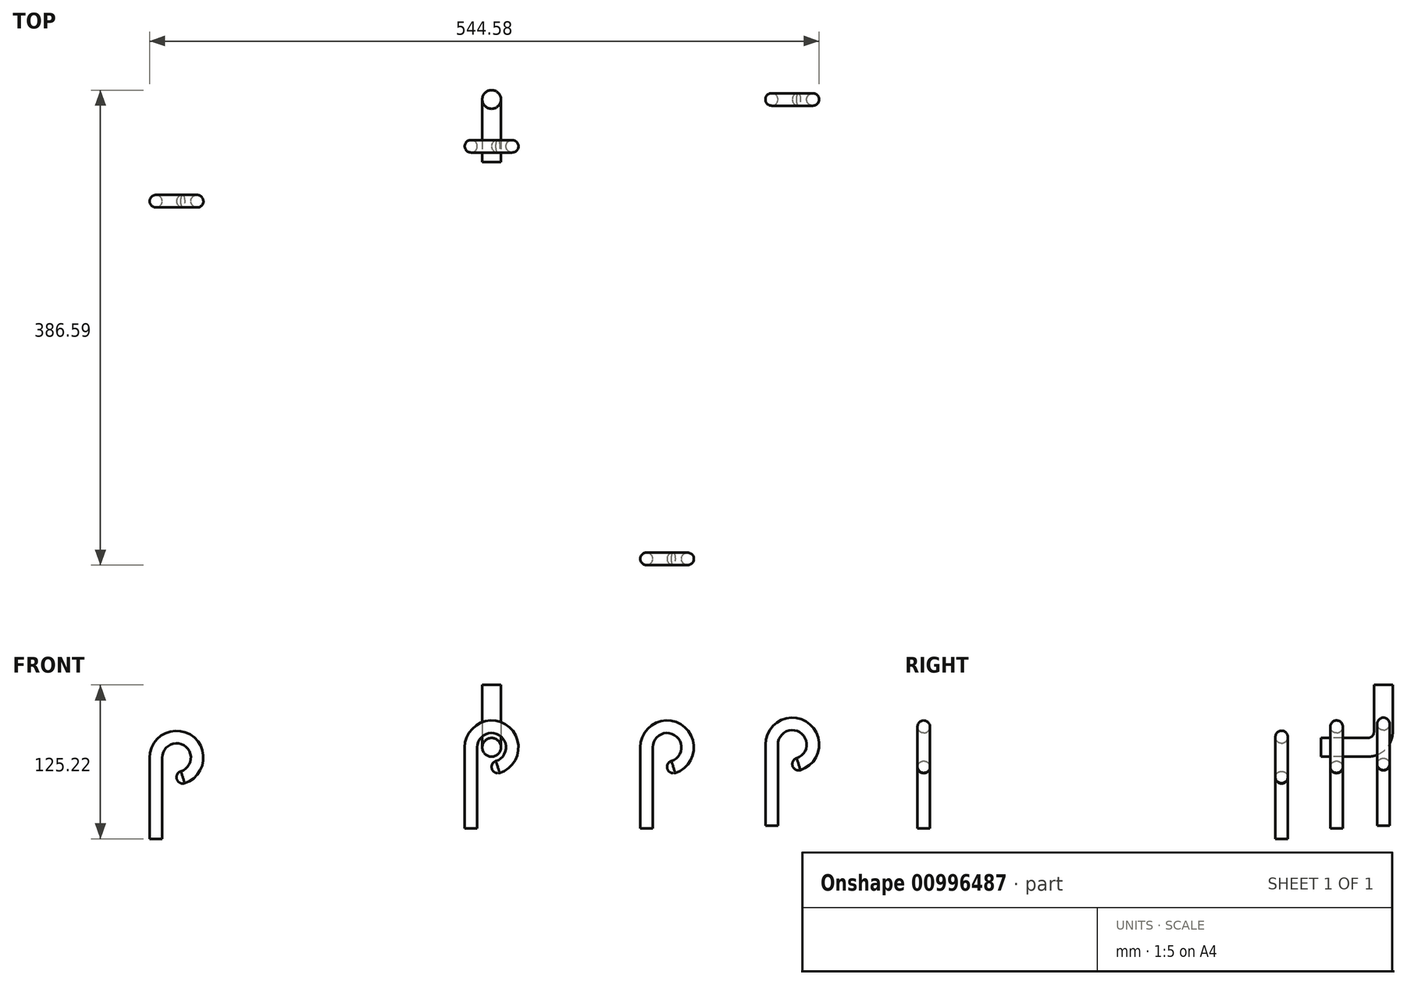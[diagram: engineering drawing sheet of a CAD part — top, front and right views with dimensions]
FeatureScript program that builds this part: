
annotation { "Feature Type Name" : "Feature", "Feature Type Description" : "" }
export const myFeature = defineFeature(function(context is Context, id is Id, definition is map)
    precondition{}
    {
        {
            var Q0;
            Q0=qCreatedBy(makeId("Front.planeOp"),FACE);
            var sketch = newSketch(context, id + "F0", { "sketchPlane" : qUnion([Q0])});
            skLineSegment(sketch, "E0", {"start": v(0, -66.04) * mm, "end": v(0, 0) * mm});
            skArc(sketch, "E1", {"start": v(33.53, 0) * mm, "mid": v(16.76, 16.76) * mm, "end": v(0, 0) * mm});
            skArc(sketch, "E2", {"start": v(16.76, -16.76) * mm, "mid": v(28.62, -11.85) * mm, "end": v(33.53, 0) * mm});
            skSolve(sketch);
        }
        {
            var Q0;
            Q0=qCreatedBy(makeId("Top.planeOp"),FACE);
            cPlane(context, id + "F1", {"entities" : qUnion([Q0]), "cplaneType" : CPlaneType.OFFSET, "offset" : 66.04 * mm, "oppositeDirection" : true, "width" : 152.4 * mm, "height" : 152.4 * mm});
        }
        {
            var Q0;
            Q0=qCreatedBy(id+"F1.planeOp",FACE);
            var sketch = newSketch(context, id + "F2", { "sketchPlane" : qUnion([Q0])});
            skCircle(sketch, "E3", {"center": v(0, 0) * mm, "radius": 5.08 * mm});
            skSolve(sketch);
        }
        {
            var Q0;
            Q0=makeQuery(id+"F2.imprint","IMPRINT",FACE,{"disambiguationData":[TD([[makeQuery(id+"F2.imprint","IMPRINT",EDGE,{"derivedFrom":sQuery(id+"F2.wireOp",EDGE,"E3")}),1.0]])]});
            var Q1;
            Q1=sQuery(id+"F0.wireOp",EDGE,"E0");
            var Q2;
            Q2=sQuery(id+"F0.wireOp",EDGE,"E1");
            var Q3;
            Q3=sQuery(id+"F0.wireOp",EDGE,"E2");
            sweep(context, id + "F3", {"profiles" : qUnion([Q0]), "path" : qUnion([Q1, Q2, Q3])});
        }
        {
            var Q0;
            Q0=qCreatedBy(makeId("Right.planeOp"),FACE);
            cPlane(context, id + "F4", {"entities" : qUnion([Q0]), "cplaneType" : CPlaneType.OFFSET, "offset" : 16.76 * mm, "width" : 152.4 * mm, "height" : 152.4 * mm});
        }
        {
            var Q0;
            Q0=qCreatedBy(id+"F4.planeOp",FACE);
            var sketch = newSketch(context, id + "F5", { "sketchPlane" : qUnion([Q0])});
            skLineSegment(sketch, "E4", {"start": v(0, 0) * mm, "end": v(25.4, 0) * mm});
            skLineSegment(sketch, "E5", {"start": v(38.1, 12.7) * mm, "end": v(38.1, 50.8) * mm});
            skLineSegment(sketch, "E6", {"start": v(0, 0) * mm, "end": v(-12.7, 0) * mm});
            skPoint(sketch, "E7.visualSharp", {"position": v(38.1, 0) * mm});
            skArc(sketch, "E7.filletArc", {"start": v(25.4, 0) * mm, "mid": v(34.38, 3.72) * mm, "end": v(38.1, 12.7) * mm});
            skSolve(sketch);
        }
        {
            var Q0;
            Q0=qCreatedBy(makeId("Top.planeOp"),FACE);
            cPlane(context, id + "F6", {"entities" : qUnion([Q0]), "cplaneType" : CPlaneType.OFFSET, "offset" : 50.8 * mm, "width" : 152.4 * mm, "height" : 152.4 * mm});
        }
        {
            var Q0;
            Q0=qCreatedBy(id+"F6.planeOp",FACE);
            var sketch = newSketch(context, id + "F7", { "sketchPlane" : qUnion([Q0])});
            skCircle(sketch, "E8", {"center": v(16.76, 38.1) * mm, "radius": 7.62 * mm});
            skSolve(sketch);
        }
        {
            var Q0;
            Q0=makeQuery(id+"F7.imprint","IMPRINT",FACE,{"disambiguationData":[TD([[makeQuery(id+"F7.imprint","IMPRINT",EDGE,{"derivedFrom":sQuery(id+"F7.wireOp",EDGE,"E8")}),1.0]])]});
            var Q1;
            Q1=sQuery(id+"F5.wireOp",EDGE,"E5");
            var Q2;
            Q2=sQuery(id+"F5.wireOp",EDGE,"E7.filletArc");
            var Q3;
            Q3=sQuery(id+"F5.wireOp",EDGE,"E6");
            var Q4;
            Q4=sQuery(id+"F5.wireOp",EDGE,"E4");
            sweep(context, id + "F8", {"profiles" : qUnion([Q0]), "path" : qUnion([Q1, Q2, Q3, Q4])});
        }
        {
            var Q0;
            Q0=makeQuery(id+"F3.opSweep","CAP_EDGE",EDGE,{"disambiguationData":[OSD([sQuery(id+"F0.wireOp",VERTEX,"E2.start"),sQuery(id+"F2.wireOp",EDGE,"E3")])],"isStart":false});
            fillet(context, id + "F9", {"entities" : qUnion([Q0]), "radius" : 5.08 * mm, "tangentPropagation" : true, "allowEdgeOverflow" : false});
        }
        {
            var Q0;
            Q0=makeQuery(id+"F3.opSweep","SWEPT_BODY",BODY,{"disambiguationData":[OSD([sQuery(id+"F0.wireOp",EDGE,"E2"),sQuery(id+"F2.wireOp",EDGE,"E3")])]});
            transform(context, id + "F10", {"entities" : qUnion([Q0]), "transformType" : TransformType.TRANSLATION_3D, "dx" : 288.8 * mm, "dy" : 0 * mm, "dz" : 0 * mm, "makeCopy" : true});
        }
        {
            var Q0;
            Q0=makeQuery(id+"F3.opSweep","SWEPT_BODY",BODY,{"disambiguationData":[OSD([sQuery(id+"F0.wireOp",EDGE,"E2"),sQuery(id+"F2.wireOp",EDGE,"E3")])]});
            transform(context, id + "F11", {"entities" : qUnion([Q0]), "transformType" : TransformType.TRANSLATION_3D, "dx" : 86.1 * mm, "dy" : -241.05 * mm, "dz" : 0 * mm, "makeCopy" : true});
        }
        {
            var Q0;
            Q0=makeQuery(id+"F3.opSweep","SWEPT_BODY",BODY,{"disambiguationData":[OSD([sQuery(id+"F0.wireOp",EDGE,"E2"),sQuery(id+"F2.wireOp",EDGE,"E3")])]});
            transform(context, id + "F12", {"entities" : qUnion([Q0]), "transformType" : TransformType.TRANSLATION_3D, "dx" : 299.97 * mm, "dy" : 266.7 * mm, "dz" : -8.38 * mm, "makeCopy" : true});
        }
        {
            var Q0;
            Q0=makeQuery(id+"F3.opSweep","SWEPT_BODY",BODY,{"disambiguationData":[OSD([sQuery(id+"F0.wireOp",EDGE,"E2"),sQuery(id+"F2.wireOp",EDGE,"E3")])]});
            var Q1;
            Q1=makeQuery(id+"F8.opSweep","SWEPT_BODY",BODY,{"disambiguationData":[OSD([sQuery(id+"F5.wireOp",EDGE,"E5"),sQuery(id+"F7.wireOp",EDGE,"E8")])]});
            transform(context, id + "F13", {"entities" : qUnion([Q0, Q1]), "transformType" : TransformType.TRANSLATION_3D, "dx" : -56.64 * mm, "dy" : 94.74 * mm, "dz" : 0 * mm, "makeCopy" : false});
        }
        {
            var Q0;
            Q0=makeQuery(id+"F10.opPattern","COPY",BODY,{"derivedFrom":makeQuery(id+"F3.opSweep","SWEPT_BODY",BODY,{"disambiguationData":[OSD([sQuery(id+"F0.wireOp",EDGE,"E2"),sQuery(id+"F2.wireOp",EDGE,"E3")])]}),"instanceName":"1"});
            transform(context, id + "F14", {"entities" : qUnion([Q0]), "transformType" : TransformType.TRANSLATION_3D, "dx" : -100.84 * mm, "dy" : 132.84 * mm, "dz" : 2.3 * mm, "makeCopy" : false});
        }
        {
            var Q0;
            Q0=makeQuery(id+"F12.opPattern","COPY",BODY,{"derivedFrom":makeQuery(id+"F3.opSweep","SWEPT_BODY",BODY,{"disambiguationData":[OSD([sQuery(id+"F0.wireOp",EDGE,"E2"),sQuery(id+"F2.wireOp",EDGE,"E3")])]}),"instanceName":"1"});
            transform(context, id + "F15", {"entities" : qUnion([Q0]), "transformType" : TransformType.TRANSLATION_3D, "dx" : -612.9 * mm, "dy" : -216.66 * mm, "dz" : 0 * mm, "makeCopy" : false});
        }
    });
